# Revit family: Sanitary_Toilets_hansgrohe_60266SVP-EluPura-Original-S-Floorstandin__00
name_source: partatom
category: Plumbing Fixtures
units: mm (PartAtom-declared; Revit-internal decimal feet)

## family parameters
Always vertical = No
Cut with Voids When Loaded = No
OmniClass Number = 23.31.19.00
OmniClass Title = Toilets
Part Type = Normal
Room Calculation Point = No
Round Connector Dimension = Use Diameter
Shared = No
Work Plane-Based = Yes

## types (1)
- 452 White
    Connector Description = Water Outlet 102 mm
    Default Elevation = 1219 mm
    Description = EluPura Original S Floorstanding WC close coupled 640 with douche and horizontal outlet rimless AquaChannel Flush(unpacked)
    Diameter = 102 mm
    Manufacturer = Hansgrohe
    Material 1 = Hansgrohe - Ceramic - 452 White
    Material 2 = Hansgrohe - Metal - 000 Chrome
    Model = 60266SVP
    Product Guid = d6e11749-1c26-4c6e-aebd-63749dd65bdc
    Product Page URL = https://www.hansgrohe.com
    Product data url = https://bimobject.com
    URL = https://www.hansgrohe.com
    Version = 1

## geometry (parser evidence)
native form markers: Sweep x2
no freeform markers — native parametric forms only
